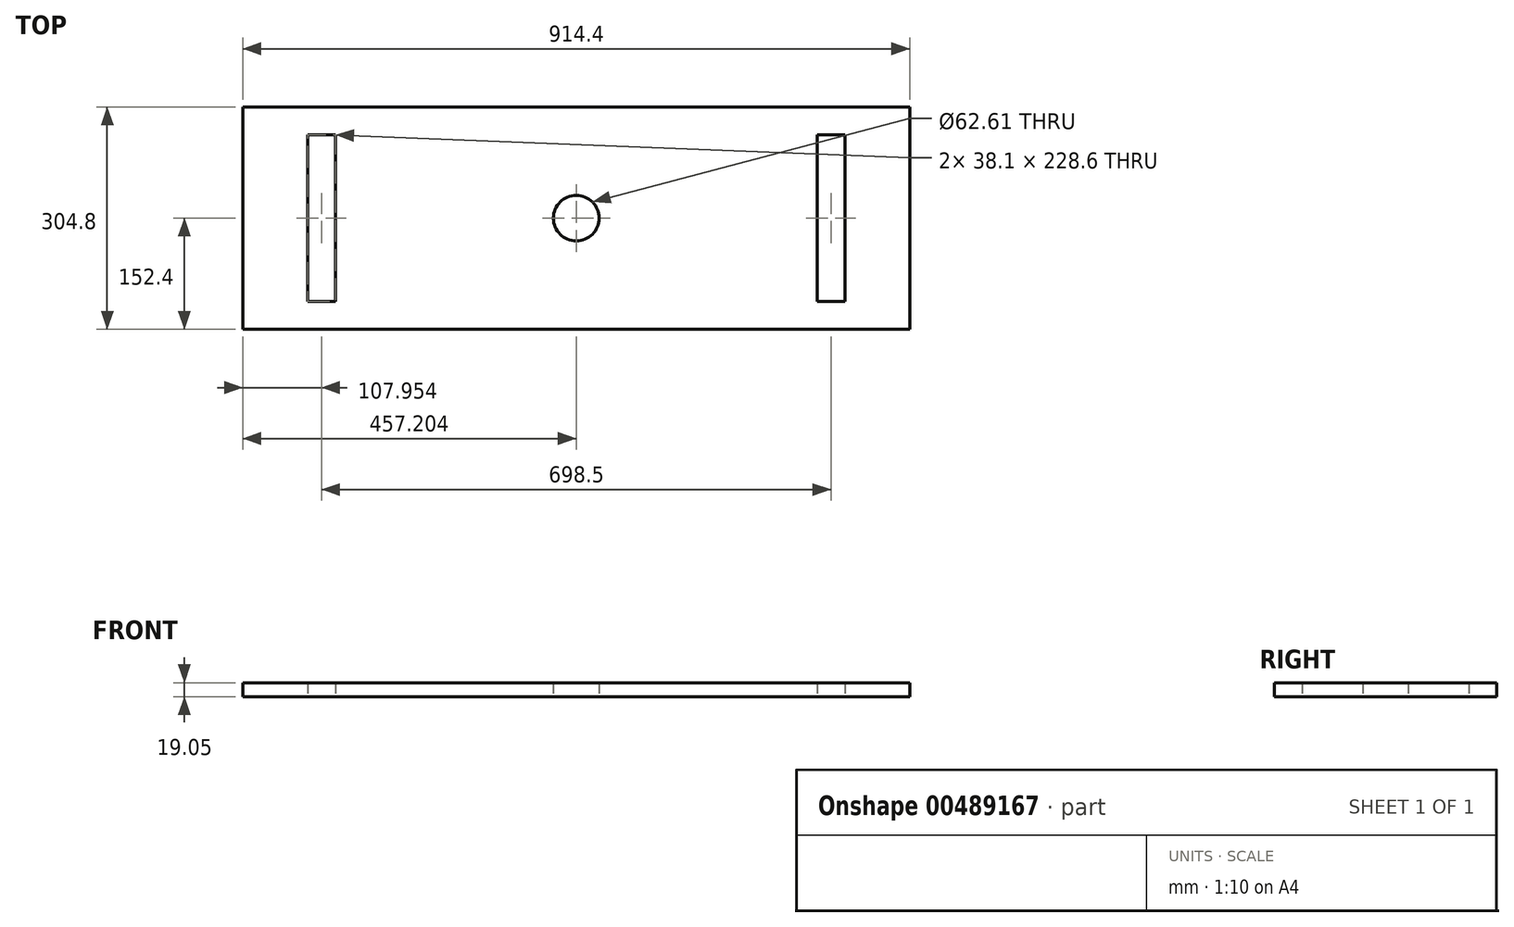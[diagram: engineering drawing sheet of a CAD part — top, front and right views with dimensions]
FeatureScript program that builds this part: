
annotation { "Feature Type Name" : "Feature", "Feature Type Description" : "" }
export const myFeature = defineFeature(function(context is Context, id is Id, definition is map)
    precondition{}
    {
        {
            var Q0;
            Q0=qCreatedBy(makeId("Top.planeOp"),FACE);
            var sketch = newSketch(context, id + "F0", { "sketchPlane" : qUnion([Q0])});
            skLineSegment(sketch, "E0.bottom", {"start": v(-464.88, 38.1) * mm, "end": v(449.52, 38.1) * mm});
            skLineSegment(sketch, "E0.top", {"start": v(-464.88, -266.7) * mm, "end": v(449.52, -266.7) * mm});
            skLineSegment(sketch, "E0.left", {"start": v(-464.88, 38.1) * mm, "end": v(-464.88, -266.7) * mm});
            skLineSegment(sketch, "E0.right", {"start": v(449.52, 38.1) * mm, "end": v(449.52, -266.7) * mm});
            skPoint(sketch, "E1.centerSnap0", {"position": v(-7.68, 38.1) * mm});
            skCircle(sketch, "E2", {"center": v(-7.68, -114.3) * mm, "radius": 31.3 * mm});
            skPoint(sketch, "E2.centerSnap0", {"position": v(-464.88, -114.3) * mm});
            skLineSegment(sketch, "E3.bottom", {"start": v(-375.98, 0) * mm, "end": v(-337.88, 0) * mm});
            skLineSegment(sketch, "E3.top", {"start": v(-375.98, -228.6) * mm, "end": v(-337.88, -228.6) * mm});
            skLineSegment(sketch, "E3.left", {"start": v(-375.98, 0) * mm, "end": v(-375.98, -228.6) * mm});
            skLineSegment(sketch, "E3.right", {"start": v(-337.88, 0) * mm, "end": v(-337.88, -228.6) * mm});
            skLineSegment(sketch, "E4.bottom", {"start": v(322.52, 0) * mm, "end": v(360.62, 0) * mm});
            skLineSegment(sketch, "E4.top", {"start": v(322.52, -228.6) * mm, "end": v(360.62, -228.6) * mm});
            skLineSegment(sketch, "E4.left", {"start": v(322.52, 0) * mm, "end": v(322.52, -228.6) * mm});
            skLineSegment(sketch, "E4.right", {"start": v(360.62, 0) * mm, "end": v(360.62, -228.6) * mm});
            skSolve(sketch);
        }
        {
            var Q0;
            Q0=makeQuery(id+"F0.imprint","IMPRINT",FACE,{"disambiguationData":[TD([[makeQuery(id+"F0.imprint","IMPRINT",EDGE,{"derivedFrom":sQuery(id+"F0.wireOp",EDGE,"E0.bottom")}),-1.0]])]});
            extrude(context, id + "F1", {"entities" : qUnion([Q0]), "depth" : 19.05 * mm, "offsetDistance" : 25.4 * mm});
        }
    });
